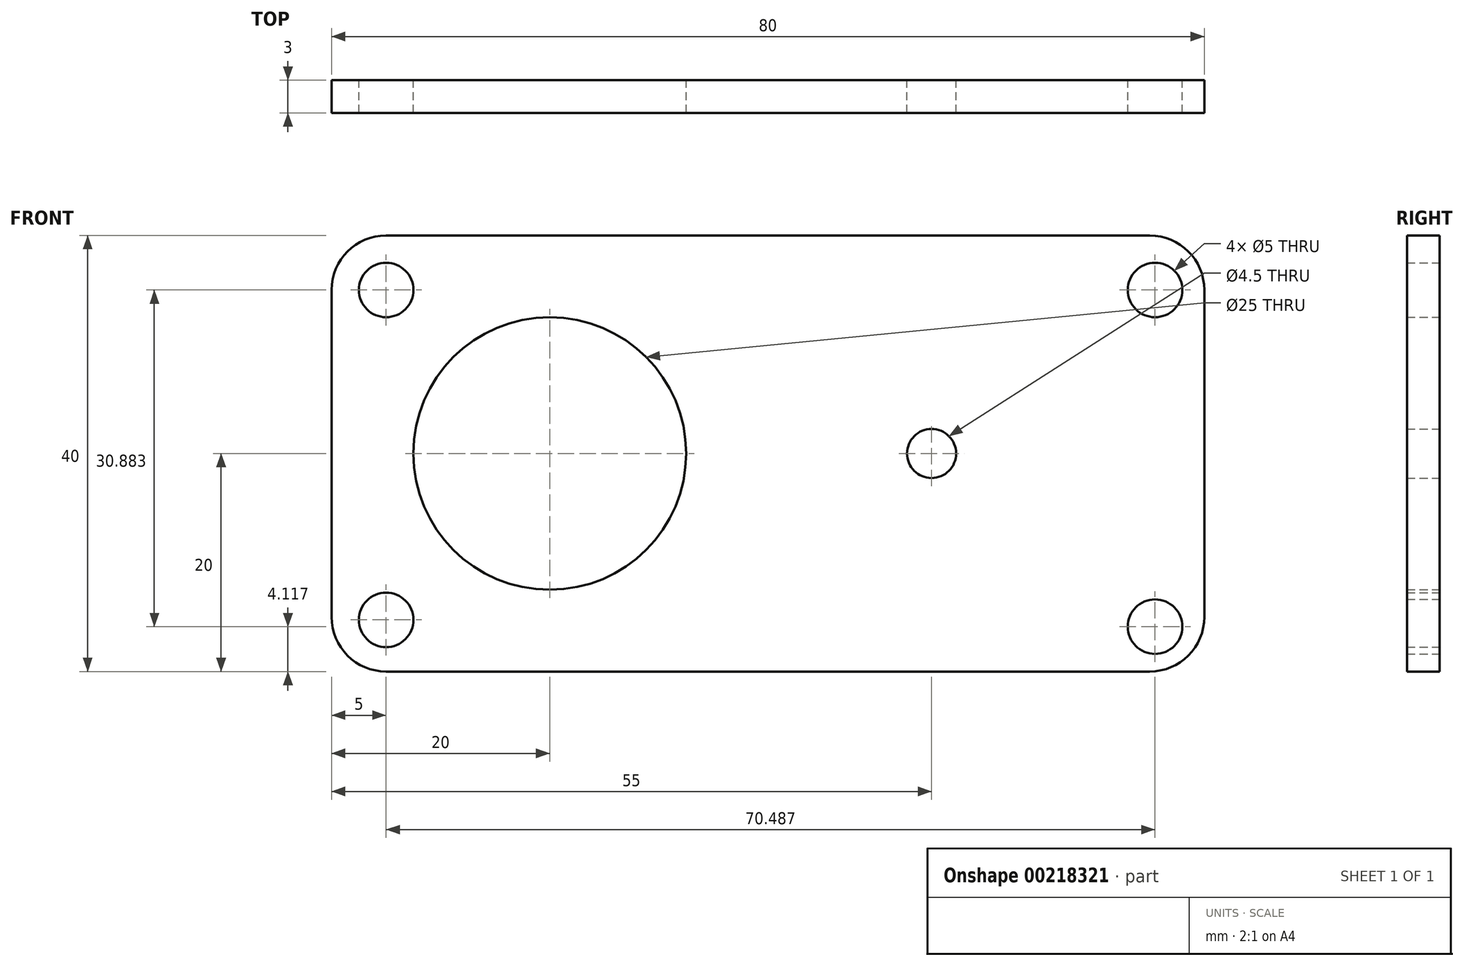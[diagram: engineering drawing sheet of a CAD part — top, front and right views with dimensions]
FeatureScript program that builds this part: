
annotation { "Feature Type Name" : "Feature", "Feature Type Description" : "" }
export const myFeature = defineFeature(function(context is Context, id is Id, definition is map)
    precondition{}
    {
        {
            var Q0;
            Q0=qCreatedBy(makeId("Front.planeOp"),FACE);
            var sketch = newSketch(context, id + "F0", { "sketchPlane" : qUnion([Q0])});
            skLineSegment(sketch, "E0.bottom", {"start": v(-40, -20) * mm, "end": v(40, -20) * mm});
            skLineSegment(sketch, "E0.top", {"start": v(-40, 20) * mm, "end": v(40, 20) * mm});
            skLineSegment(sketch, "E0.left", {"start": v(-40, -20) * mm, "end": v(-40, 20) * mm});
            skLineSegment(sketch, "E0.right", {"start": v(40, -20) * mm, "end": v(40, 20) * mm});
            skPoint(sketch, "E0.middle", {"position": v(0, 0) * mm});
            skCircle(sketch, "E1", {"center": v(-35, 15) * mm, "radius": 2.5 * mm});
            skCircle(sketch, "E2", {"center": v(-20, 0) * mm, "radius": 12.5 * mm});
            skCircle(sketch, "E3", {"center": v(15, 0) * mm, "radius": 2.25 * mm});
            skCircle(sketch, "E4", {"center": v(-35, -15.26) * mm, "radius": 2.5 * mm});
            skCircle(sketch, "E5", {"center": v(35.49, 15) * mm, "radius": 2.5 * mm});
            skCircle(sketch, "E6", {"center": v(35.49, -15.88) * mm, "radius": 2.5 * mm});
            skSolve(sketch);
        }
        {
            var Q0;
            Q0=makeQuery(id+"F0.imprint","IMPRINT",FACE,{"disambiguationData":[TD([[makeQuery(id+"F0.imprint","IMPRINT",EDGE,{"derivedFrom":sQuery(id+"F0.wireOp",EDGE,"E0.bottom")}),1.0]])]});
            extrude(context, id + "F1", {"entities" : qUnion([Q0]), "depth" : 3 * mm, "offsetDistance" : 25 * mm});
        }
        {
            var Q0;
            Q0=makeQuery(id+"F1.opExtrude","SWEPT_EDGE",EDGE,{"disambiguationData":[OSD([sQuery(id+"F0.wireOp",EDGE,"E0.top"),sQuery(id+"F0.wireOp",EDGE,"E0.left")])]});
            var Q1;
            Q1=makeQuery(id+"F1.opExtrude","SWEPT_EDGE",EDGE,{"disambiguationData":[OSD([sQuery(id+"F0.wireOp",EDGE,"E0.top"),sQuery(id+"F0.wireOp",EDGE,"E0.right")])]});
            var Q2;
            Q2=makeQuery(id+"F1.opExtrude","SWEPT_EDGE",EDGE,{"disambiguationData":[OSD([sQuery(id+"F0.wireOp",EDGE,"E0.bottom"),sQuery(id+"F0.wireOp",EDGE,"E0.right")])]});
            var Q3;
            Q3=makeQuery(id+"F1.opExtrude","SWEPT_EDGE",EDGE,{"disambiguationData":[OSD([sQuery(id+"F0.wireOp",EDGE,"E0.bottom"),sQuery(id+"F0.wireOp",EDGE,"E0.left")])]});
            fillet(context, id + "F2", {"entities" : qUnion([Q0, Q1, Q2, Q3]), "radius" : 5 * mm, "tangentPropagation" : true, "allowEdgeOverflow" : false});
        }
    });
